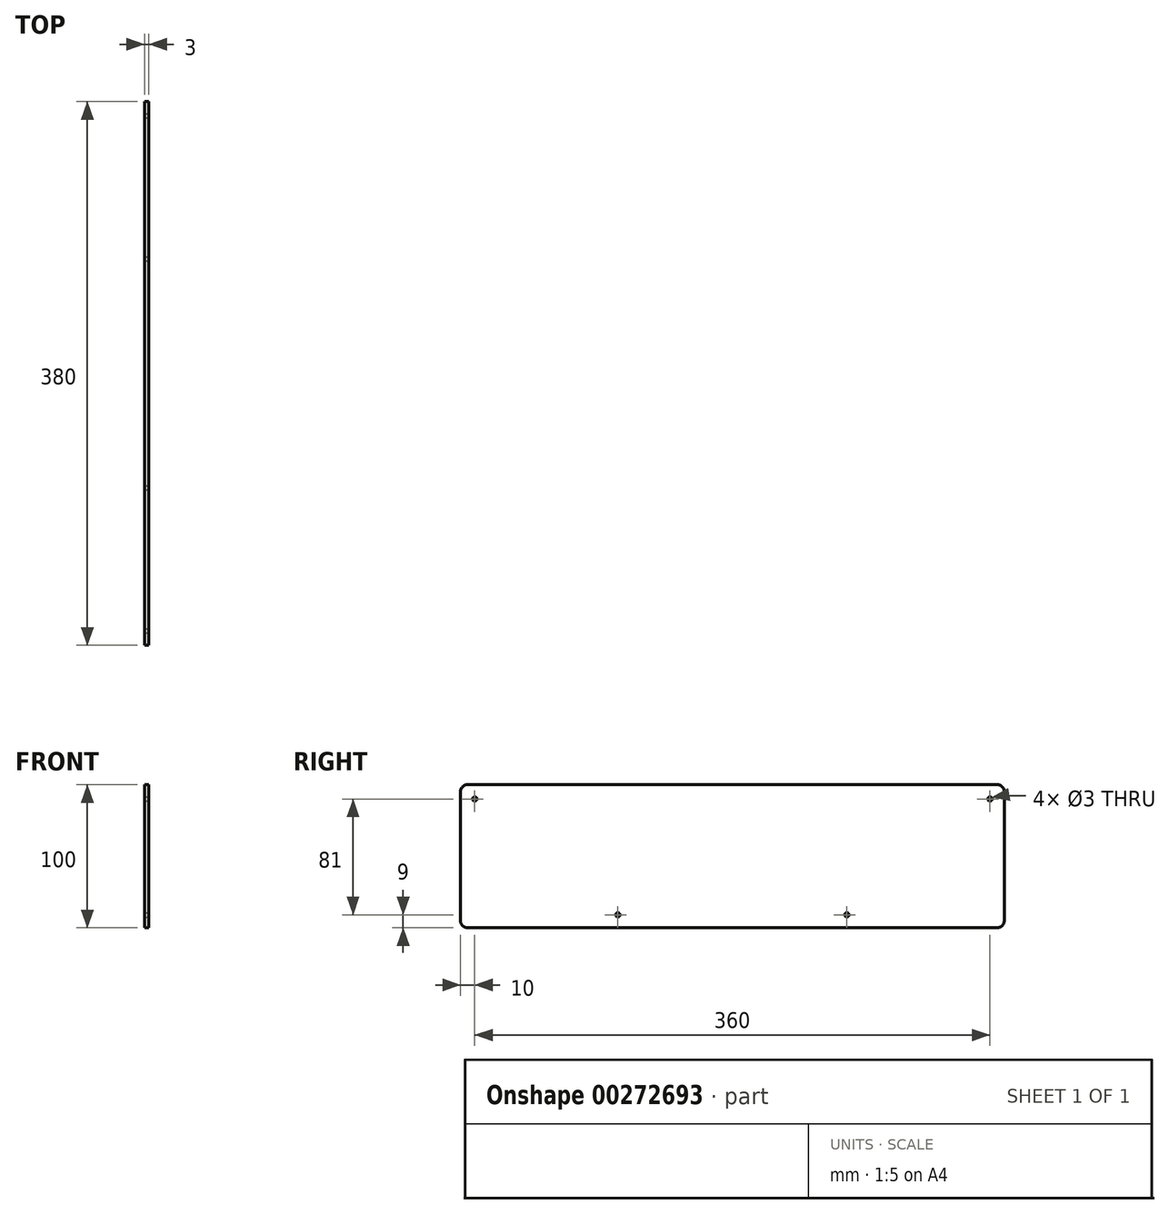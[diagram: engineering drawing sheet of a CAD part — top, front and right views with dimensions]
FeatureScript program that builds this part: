
annotation { "Feature Type Name" : "Feature", "Feature Type Description" : "" }
export const myFeature = defineFeature(function(context is Context, id is Id, definition is map)
    precondition{}
    {
        {
            var Q0;
            Q0=qCreatedBy(makeId("Top.planeOp"),FACE);
            var sketch = newSketch(context, id + "F0", { "sketchPlane" : qUnion([Q0])});
            skLineSegment(sketch, "E0.bottom", {"start": v(0, -190) * mm, "end": v(-3, -190) * mm});
            skLineSegment(sketch, "E0.top", {"start": v(0, 190) * mm, "end": v(-3, 190) * mm});
            skLineSegment(sketch, "E0.left", {"start": v(0, -190) * mm, "end": v(0, 190) * mm});
            skLineSegment(sketch, "E0.right", {"start": v(-3, -190) * mm, "end": v(-3, 190) * mm});
            skSolve(sketch);
        }
        {
            var Q0;
            Q0=makeQuery(id+"F0.imprint","IMPRINT",FACE,{"disambiguationData":[TD([[makeQuery(id+"F0.imprint","IMPRINT",EDGE,{"derivedFrom":sQuery(id+"F0.wireOp",EDGE,"E0.bottom")}),-1.0]])]});
            extrude(context, id + "F1", {"entities" : qUnion([Q0]), "depth" : 100 * mm});
        }
        {
            var Q0;
            Q0=makeQuery(id+"F1.opExtrude","CAP_EDGE",EDGE,{"disambiguationData":[OSD([sQuery(id+"F0.wireOp",EDGE,"E0.bottom")])],"isStart":false});
            var Q1;
            Q1=makeQuery(id+"F1.opExtrude","CAP_EDGE",EDGE,{"disambiguationData":[OSD([sQuery(id+"F0.wireOp",EDGE,"E0.bottom")])],"isStart":true});
            var Q2;
            Q2=makeQuery(id+"F1.opExtrude","CAP_EDGE",EDGE,{"disambiguationData":[OSD([sQuery(id+"F0.wireOp",EDGE,"E0.top")])],"isStart":true});
            var Q3;
            Q3=makeQuery(id+"F1.opExtrude","CAP_EDGE",EDGE,{"disambiguationData":[OSD([sQuery(id+"F0.wireOp",EDGE,"E0.top")])],"isStart":false});
            fillet(context, id + "F2", {"entities" : qUnion([Q0, Q1, Q2, Q3]), "radius" : 5 * mm, "tangentPropagation" : true, "allowEdgeOverflow" : false});
        }
        {
            var Q0;
            Q0=makeQuery(id+"F1.opExtrude","SWEPT_FACE",FACE,{"disambiguationData":[OSD([sQuery(id+"F0.wireOp",EDGE,"E0.left")])]});
            var sketch = newSketch(context, id + "F3", { "sketchPlane" : qUnion([Q0])});
            skPoint(sketch, "E1", {"position": v(-180, 90) * mm});
            skPoint(sketch, "E2", {"position": v(-80, 9) * mm});
            skPoint(sketch, "E3", {"position": v(80, 9) * mm});
            skLineSegment(sketch, "E4", {"start": v(0, 0) * mm, "end": v(0, 100) * mm, "construction": true});
            skPoint(sketch, "E5.MirrorP", {"position": v(180, 90) * mm});
            skSolve(sketch);
        }
        {
            var Q0;
            Q0=sQuery(id+"F3.wireOp",VERTEX,"E5.MirrorP");
            var Q1;
            Q1=sQuery(id+"F3.wireOp",VERTEX,"E3");
            var Q2;
            Q2=sQuery(id+"F3.wireOp",VERTEX,"E2");
            var Q3;
            Q3=sQuery(id+"F3.wireOp",VERTEX,"E1");
            var Q4;
            Q4=makeQuery(id+"F1.opExtrude","SWEPT_BODY",BODY,{"disambiguationData":[OSD([sQuery(id+"F0.wireOp",EDGE,"E0.bottom"),sQuery(id+"F0.wireOp",EDGE,"E0.top"),sQuery(id+"F0.wireOp",EDGE,"E0.left"),sQuery(id+"F0.wireOp",EDGE,"E0.right")])]});
            hole(context, id + "F4", {"style" : HoleStyle.SIMPLE, "endStyle" : HoleEndStyle.THROUGH, "holeDiameter" : 3 * mm, "majorDiameter" : 5 * mm, "isTappedThrough" : true, "tappedDepth" : 12 * mm, "tapClearance" : 3, "startFromSketch" : true, "locations" : qUnion([Q0, Q1, Q2, Q3]), "scope" : qUnion([Q4])});
        }
    });
